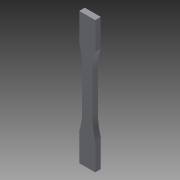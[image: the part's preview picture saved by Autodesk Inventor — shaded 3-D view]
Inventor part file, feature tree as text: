
AUTODESK INVENTOR PART (.ipt)
format: ipt  version: 2014 SP1 (Build 180222100, 222)  size: 83,456 bytes
history: native  units: mm
features: extrude x1, sketch x1
ambient origin geometry x8: Origin, YZ Plane, XZ Plane, XY Plane, X Axis, Y Axis, Z Axis, Center Point
bodies: Solid1 (feature_tree)
feature tree (2):
  extrude  "Extrusion1"  Depth=76.0mm
  sketch  "Sketch1"  dims[d2=20.0mm d5=76.0mm d6=76.0mm d7=82.5mm d8=13.0mm d9=25.0mm d10=7.0mm d11=0.0mm]
